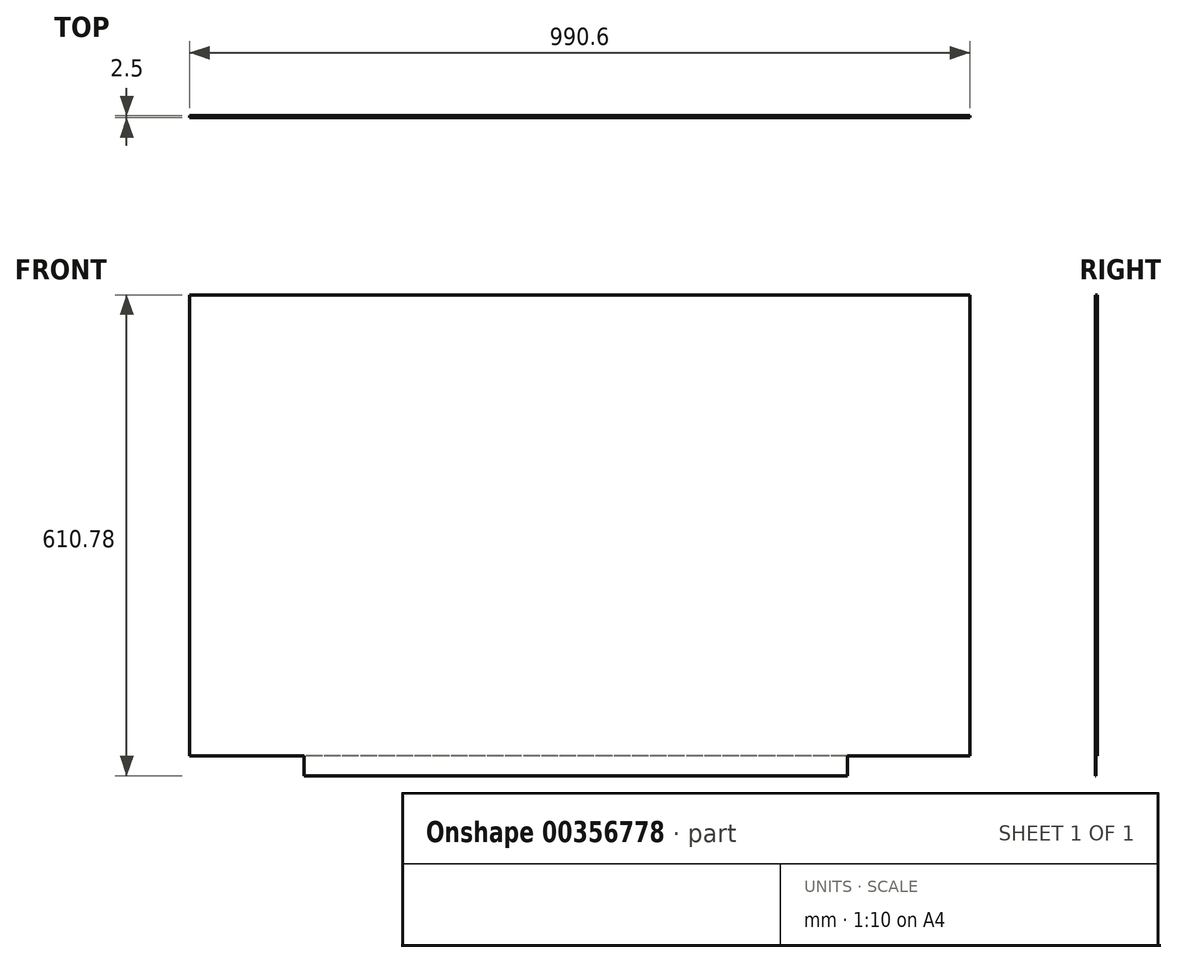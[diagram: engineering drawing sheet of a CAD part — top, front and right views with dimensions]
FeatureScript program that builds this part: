
annotation { "Feature Type Name" : "Feature", "Feature Type Description" : "" }
export const myFeature = defineFeature(function(context is Context, id is Id, definition is map)
    precondition{}
    {
        {
            var Q0;
            Q0=qCreatedBy(makeId("Front.planeOp"),FACE);
            var sketch = newSketch(context, id + "F0", { "sketchPlane" : qUnion([Q0])});
            skLineSegment(sketch, "E0.bottom", {"start": v(495.3, 292.9) * mm, "end": v(-495.3, 292.9) * mm});
            skLineSegment(sketch, "E0.top", {"start": v(495.3, -292.9) * mm, "end": v(-495.3, -292.9) * mm});
            skLineSegment(sketch, "E0.left", {"start": v(495.3, 292.9) * mm, "end": v(495.3, -292.9) * mm});
            skLineSegment(sketch, "E0.right", {"start": v(-495.3, 292.9) * mm, "end": v(-495.3, -292.9) * mm});
            skPoint(sketch, "E0.middle", {"position": v(0, 0) * mm});
            skSolve(sketch);
        }
        {
            var Q0;
            Q0 = qSketchRegion(id + "F0", true);
            extrude(context, id + "F1", {"entities" : qUnion([Q0]), "depth" : 2.5 * mm});
        }
        {
            var Q0;
            Q0=makeQuery(id+"F1.opExtrude","CAP_FACE",FACE,{"disambiguationData":[OSD([sQuery(id+"F0.wireOp",EDGE,"E0.bottom"),sQuery(id+"F0.wireOp",EDGE,"E0.top"),sQuery(id+"F0.wireOp",EDGE,"E0.left"),sQuery(id+"F0.wireOp",EDGE,"E0.right")])],"isStart":false});
            var sketch = newSketch(context, id + "F2", { "sketchPlane" : qUnion([Q0])});
            skLineSegment(sketch, "E1.bottom", {"start": v(-350.3, -292.9) * mm, "end": v(340.3, -292.9) * mm});
            skLineSegment(sketch, "E1.top", {"start": v(-350.3, -317.9) * mm, "end": v(340.3, -317.9) * mm});
            skLineSegment(sketch, "E1.left", {"start": v(-350.3, -292.9) * mm, "end": v(-350.3, -317.9) * mm});
            skLineSegment(sketch, "E1.right", {"start": v(340.3, -292.9) * mm, "end": v(340.3, -317.9) * mm});
            skSolve(sketch);
        }
        {
            var Q0;
            Q0 = qSketchRegion(id + "F2", true);
            extrude(context, id + "F3", {"entities" : qUnion([Q0]), "operationType" : NewBodyOperationType.ADD, "oppositeDirection" : true, "depth" : 0.5 * mm});
        }
    });
